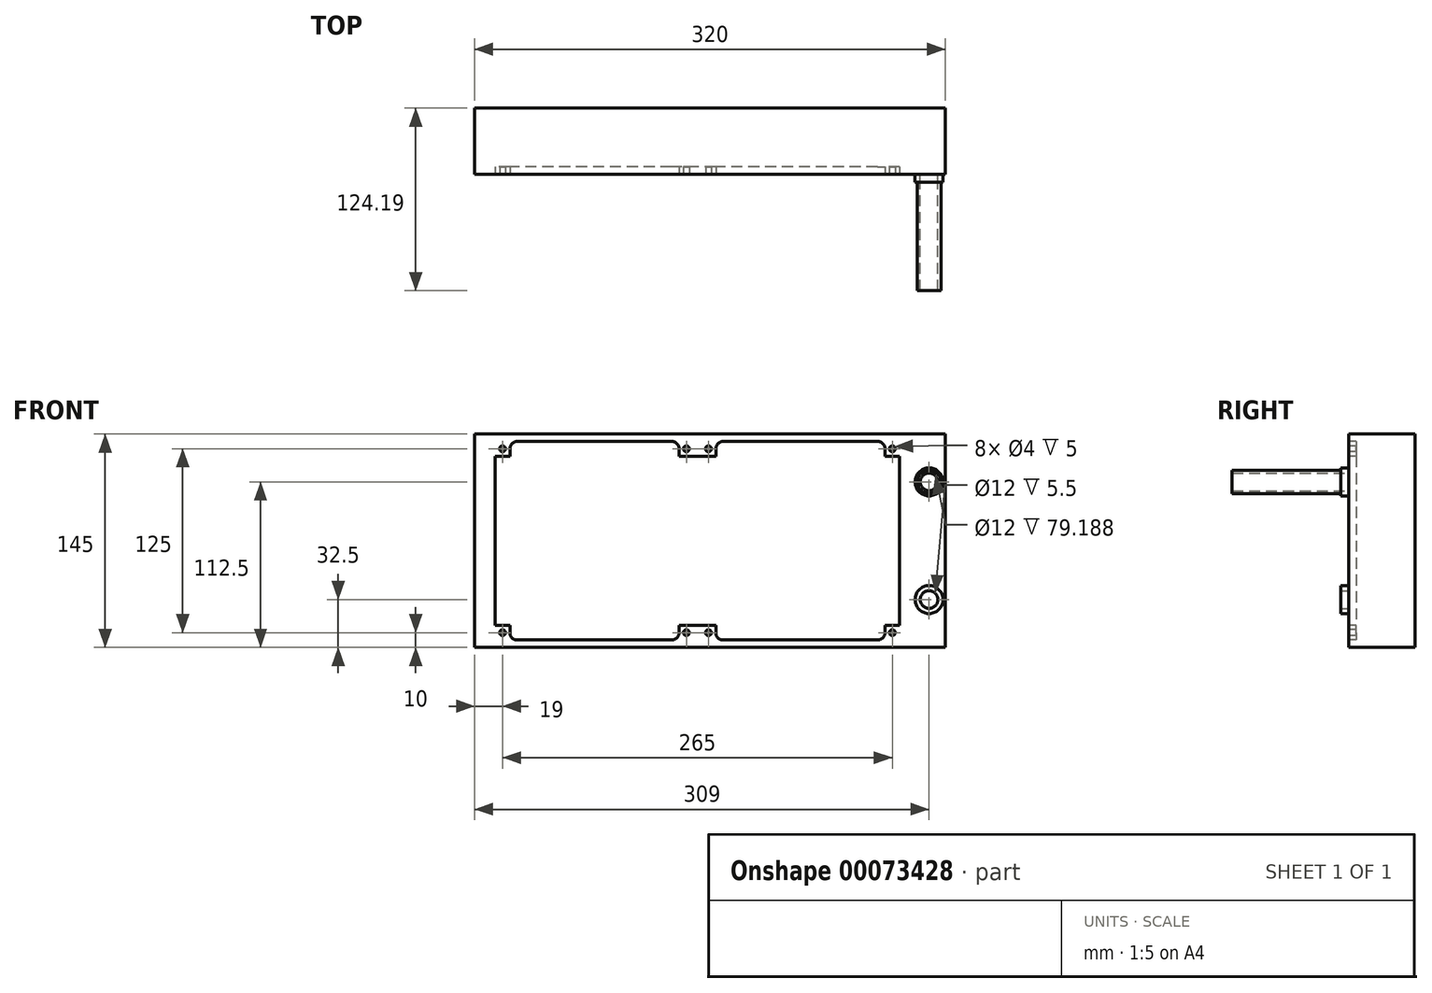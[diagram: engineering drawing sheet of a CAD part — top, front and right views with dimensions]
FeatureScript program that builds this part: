
annotation { "Feature Type Name" : "Feature", "Feature Type Description" : "" }
export const myFeature = defineFeature(function(context is Context, id is Id, definition is map)
    precondition{}
    {
        {
            var Q0;
            Q0=qCreatedBy(makeId("Front.planeOp"),FACE);
            var sketch = newSketch(context, id + "F0", { "sketchPlane" : qUnion([Q0])});
            skLineSegment(sketch, "E0.bottom", {"start": v(0, 72.5) * mm, "end": v(320, 72.5) * mm});
            skLineSegment(sketch, "E0.top", {"start": v(0, -72.5) * mm, "end": v(320, -72.5) * mm});
            skLineSegment(sketch, "E0.left", {"start": v(0, 72.5) * mm, "end": v(0, -72.5) * mm});
            skLineSegment(sketch, "E0.right", {"start": v(320, 72.5) * mm, "end": v(320, -72.5) * mm});
            skSolve(sketch);
        }
        {
            var Q0;
            Q0 = qSketchRegion(id + "F0", true);
            extrude(context, id + "F1", {"entities" : qUnion([Q0]), "depth" : 45 * mm});
        }
        {
            var Q0;
            Q0=makeQuery(id+"F1.opExtrude","CAP_FACE",FACE,{"disambiguationData":[OSD([sQuery(id+"F0.wireOp",EDGE,"E0.bottom"),sQuery(id+"F0.wireOp",EDGE,"E0.top"),sQuery(id+"F0.wireOp",EDGE,"E0.left"),sQuery(id+"F0.wireOp",EDGE,"E0.right")])],"isStart":false});
            var sketch = newSketch(context, id + "F2", { "sketchPlane" : qUnion([Q0])});
            skCircle(sketch, "E1", {"center": v(309, -40) * mm, "radius": 9.5 * mm});
            skCircle(sketch, "E2", {"center": v(309, 40) * mm, "radius": 9.5 * mm});
            skLineSegment(sketch, "E3", {"start": v(0, 0) * mm, "end": v(320, 0) * mm, "construction": true});
            skCircle(sketch, "E4", {"center": v(309, 40) * mm, "radius": 6 * mm});
            skCircle(sketch, "E5", {"center": v(309, -40) * mm, "radius": 6 * mm});
            skSolve(sketch);
        }
        {
            var Q0;
            Q0 = qSketchRegion(id + "F2", true);
            extrude(context, id + "F3", {"entities" : qUnion([Q0]), "operationType" : NewBodyOperationType.ADD, "depth" : 5.5 * mm});
        }
        {
            var Q0;
            {var subQ0=sQuery(id+"F0.wireOp",EDGE,"E0.right");var subQ1=sQuery(id+"F0.wireOp",EDGE,"E0.left");var subQ2=sQuery(id+"F0.wireOp",EDGE,"E0.top");var subQ3=sQuery(id+"F0.wireOp",EDGE,"E0.bottom");Q0=makeQuery(id+"F3.boolean.opBoolean","SPLIT",FACE,{"disambiguationData":[TD([makeQuery(id+"F1.opExtrude","SWEPT_FACE",FACE,{"disambiguationData":[OSD([subQ3])]})])],"derivedFrom":makeQuery(id+"F1.opExtrude","CAP_FACE",FACE,{"disambiguationData":[OSD([subQ3,subQ2,subQ1,subQ0])],"isStart":false})});}
            var sketch = newSketch(context, id + "F4", { "sketchPlane" : qUnion([Q0])});
            skCircle(sketch, "E6", {"center": v(19, 62.5) * mm, "radius": 2 * mm});
            skCircle(sketch, "E7", {"center": v(144, 62.5) * mm, "radius": 2 * mm});
            skCircle(sketch, "E8", {"center": v(159, 62.5) * mm, "radius": 2 * mm});
            skCircle(sketch, "E9", {"center": v(284, 62.5) * mm, "radius": 2 * mm});
            skLineSegment(sketch, "E10", {"start": v(14, 57.5) * mm, "end": v(14, 0) * mm});
            skLineSegment(sketch, "E11", {"start": v(289, 0) * mm, "end": v(289, 57.5) * mm});
            skLineSegment(sketch, "E12", {"start": v(289, 57.5) * mm, "end": v(279, 57.5) * mm});
            skLineSegment(sketch, "E13", {"start": v(279, 57.5) * mm, "end": v(279, 62.5) * mm});
            skLineSegment(sketch, "E14", {"start": v(274, 67.5) * mm, "end": v(169, 67.5) * mm});
            skLineSegment(sketch, "E15", {"start": v(164, 62.5) * mm, "end": v(164, 57.5) * mm});
            skLineSegment(sketch, "E16", {"start": v(164, 57.5) * mm, "end": v(139, 57.5) * mm});
            skLineSegment(sketch, "E17", {"start": v(139, 57.5) * mm, "end": v(139, 62.5) * mm});
            skLineSegment(sketch, "E18", {"start": v(134, 67.5) * mm, "end": v(29, 67.5) * mm});
            skLineSegment(sketch, "E19", {"start": v(24, 62.5) * mm, "end": v(24, 57.5) * mm});
            skLineSegment(sketch, "E20", {"start": v(24, 57.5) * mm, "end": v(14, 57.5) * mm});
            skLineSegment(sketch, "E21", {"start": v(0, 0) * mm, "end": v(320, 0) * mm, "construction": true});
            skPoint(sketch, "E22.visualSharp", {"position": v(164, 67.5) * mm});
            skArc(sketch, "E22.filletArc", {"start": v(169, 67.5) * mm, "mid": v(165.46, 66.04) * mm, "end": v(164, 62.5) * mm});
            skPoint(sketch, "E23.visualSharp", {"position": v(139, 67.5) * mm});
            skArc(sketch, "E23.filletArc", {"start": v(139, 62.5) * mm, "mid": v(137.54, 66.04) * mm, "end": v(134, 67.5) * mm});
            skPoint(sketch, "E24.visualSharp", {"position": v(279, 67.5) * mm});
            skArc(sketch, "E24.filletArc", {"start": v(279, 62.5) * mm, "mid": v(277.54, 66.04) * mm, "end": v(274, 67.5) * mm});
            skPoint(sketch, "E25.visualSharp", {"position": v(24, 67.5) * mm});
            skArc(sketch, "E25.filletArc", {"start": v(29, 67.5) * mm, "mid": v(25.46, 66.04) * mm, "end": v(24, 62.5) * mm});
            skCircle(sketch, "E26.MirrorC", {"center": v(284, -62.5) * mm, "radius": 2 * mm});
            skLineSegment(sketch, "E27.MirrorCS", {"start": v(289, 0) * mm, "end": v(289, -57.5) * mm});
            skLineSegment(sketch, "E28.MirrorCS", {"start": v(289, -57.5) * mm, "end": v(279, -57.5) * mm});
            skLineSegment(sketch, "E29.MirrorCS", {"start": v(279, -57.5) * mm, "end": v(279, -62.5) * mm});
            skArc(sketch, "E30.MirrorCS", {"start": v(279, -62.5) * mm, "mid": v(277.54, -66.04) * mm, "end": v(274, -67.5) * mm});
            skLineSegment(sketch, "E31.MirrorCS", {"start": v(274, -67.5) * mm, "end": v(169, -67.5) * mm});
            skArc(sketch, "E32.MirrorCS", {"start": v(169, -67.5) * mm, "mid": v(165.46, -66.04) * mm, "end": v(164, -62.5) * mm});
            skLineSegment(sketch, "E33.MirrorCS", {"start": v(164, -62.5) * mm, "end": v(164, -57.5) * mm});
            skCircle(sketch, "E34.MirrorC", {"center": v(159, -62.5) * mm, "radius": 2 * mm});
            skCircle(sketch, "E35.MirrorC", {"center": v(144, -62.5) * mm, "radius": 2 * mm});
            skLineSegment(sketch, "E36.MirrorCS", {"start": v(164, -57.5) * mm, "end": v(139, -57.5) * mm});
            skCircle(sketch, "E37.MirrorC", {"center": v(19, -62.5) * mm, "radius": 2 * mm});
            skLineSegment(sketch, "E38.MirrorCS", {"start": v(139, -57.5) * mm, "end": v(139, -62.5) * mm});
            skArc(sketch, "E39.MirrorCS", {"start": v(139, -62.5) * mm, "mid": v(137.54, -66.04) * mm, "end": v(134, -67.5) * mm});
            skLineSegment(sketch, "E40.MirrorCS", {"start": v(134, -67.5) * mm, "end": v(29, -67.5) * mm});
            skArc(sketch, "E41.MirrorCS", {"start": v(29, -67.5) * mm, "mid": v(25.46, -66.04) * mm, "end": v(24, -62.5) * mm});
            skLineSegment(sketch, "E42.MirrorCS", {"start": v(24, -62.5) * mm, "end": v(24, -57.5) * mm});
            skLineSegment(sketch, "E43.MirrorCS", {"start": v(14, -57.5) * mm, "end": v(14, 0) * mm});
            skLineSegment(sketch, "E44.MirrorCS", {"start": v(24, -57.5) * mm, "end": v(14, -57.5) * mm});
            skSolve(sketch);
        }
        {
            var Q0;
            Q0 = qSketchRegion(id + "F4", true);
            extrude(context, id + "F5", {"entities" : qUnion([Q0]), "operationType" : NewBodyOperationType.REMOVE, "oppositeDirection" : true, "depth" : 5 * mm});
        }
        {
            var Q0;
            {var subQ0=sQuery(id+"F0.wireOp",EDGE,"E0.right");var subQ1=sQuery(id+"F0.wireOp",EDGE,"E0.left");var subQ2=sQuery(id+"F0.wireOp",EDGE,"E0.top");var subQ3=sQuery(id+"F0.wireOp",EDGE,"E0.bottom");Q0=makeQuery(id+"F3.boolean.opBoolean","SPLIT",FACE,{"disambiguationData":[TD([makeQuery(id+"F1.opExtrude","SWEPT_FACE",FACE,{"disambiguationData":[OSD([subQ3])]})])],"derivedFrom":makeQuery(id+"F1.opExtrude","CAP_FACE",FACE,{"disambiguationData":[OSD([subQ3,subQ2,subQ1,subQ0])],"isStart":false})});}
            cPlane(context, id + "F6", {"entities" : qUnion([Q0]), "cplaneType" : CPlaneType.OFFSET, "offset" : (45 / 2) * mm, "oppositeDirection" : true, "width" : 150 * mm, "height" : 150 * mm});
        }
        {
            var Q0;
            Q0=makeQuery(id+"F3.opExtrude","CAP_FACE",FACE,{"disambiguationData":[OSD([sQuery(id+"F2.wireOp",EDGE,"E2"),sQuery(id+"F2.wireOp",EDGE,"E4")])],"isStart":false});
            var sketch = newSketch(context, id + "F7", { "sketchPlane" : qUnion([Q0])});
            skCircle(sketch, "E45", {"center": v(309, 40) * mm, "radius": 6 * mm});
            skCircle(sketch, "E46", {"center": v(309, 40) * mm, "radius": 8 * mm});
            skSolve(sketch);
        }
        {
            var Q0;
            Q0 = qSketchRegion(id + "F7", true);
            extrude(context, id + "F8", {"entities" : qUnion([Q0]), "operationType" : NewBodyOperationType.ADD, "depth" : 73.69 * mm});
        }
    });
